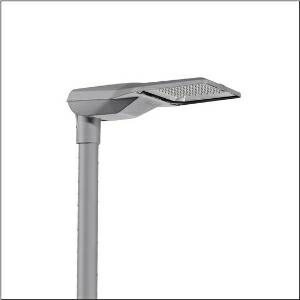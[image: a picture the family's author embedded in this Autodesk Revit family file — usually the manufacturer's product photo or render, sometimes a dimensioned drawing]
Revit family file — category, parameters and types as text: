
# Revit family: streetlight_sl_21_iq_midi___stw1_0a_5xe3e61d08nb_dcea
name_source: partatom
category: Lighting Fixtures
units: mm (PartAtom-declared; Revit-internal decimal feet)

## family parameters
Cut with Voids When Loaded = No
Host = Face
Light Source = No
Part Type = Normal
Room Calculation Point = No
Round Connector Dimension = Use Diameter
Shared = No

## types (1)
- --- (1 x LED, 20820 lm, 155.5 W, 2700K)
    Apparent Load = 155 VA
    CIE Flux Codes = 39 75 98 100 100
    Color Rendering = 70
    Color Temperature = 2700K
    Default Elevation = 1800 mm
    Description = Streetlight SL 21 iQ midi, mast luminaire, primary light control with lens, of PMMA, primary optical cover: cover, of toughened safety glass, transparent, light distribution: STW1.0a, light emission: direct distribution, primary light characteristic: asymmetric, installation type: post-top, side-entry, LED, High Power LED, rated luminous flux: 20.820lm, luminous efficacy: 134lm/W, light colour: 727, colour temperature: 2700K, control gear: iQ-Comfort, control: Auto-Match, Temp-Guard, Lumen-Switch, Night-Set, Smart-Wire, Light-Fading, Desk-Remote (wireless, voltage-free reading and setting of iQ features in the workshop via application-optimized NFC function/RFID function), optimised constant luminous flux control (CLO 2.0), pre-setting: linear dimming characteristic, mains connection: 230..240V, AC, 50/60Hz, start of lifetime: 156W, end of service life: 162W, reduction: 69W, luminaire housing, of diecast aluminium, powder-coated, Siteco® metallic grey (DB 702S), corrosivity category C5 mid according to DIN EN ISO 12944, please order mast flange separately, inclination adjustable: 0°, 5°, 10°, 15°, sealing non-destructively replaceable, multi-level sealing system, length: 644mm, width: 335mm, height: 110mm, mast flange for spigot size: 42mm (side-entry): 5XC10008XM4, 60/48mm (side-entry/post-top): 5XC10108XM2, 76/60mm (side-entry/post-top): 5XC10108XM1, mounting height: 4..8m, protection rating (complete): IP66, insulation class (complete): insulation class II (safety insulation), certification: CE, ENEC, ENEC+, VDE, impact resistance: IK10, permissible operating ambient temperature for outdoor applications: -40..+50°C, standard-compliant lighting for roads and squares, packaging unit: 1 piece

Light Distribution: STW1.0a
    Height = 111 mm
    Lamp = 1 x LED
    Lamp Light Flux = 20820 lm
    Lamp Power = 155.5 W
    Lamp count = 1
    Length = 644 mm
    Luminous efficacy = 134 lm/W
    Manufacturer = Siteco
    ModVariant = No
    Model = 5XE3E61D08NB
    Number of Poles = 1
    OnlyDefault = Yes
    Power Factor = 1
    Product Name = Streetlight SL 21 iQ midi | STW1.0a
    Product group = mast luminaire | pylon top
    ProductGroupID = 6100
    Protection Class = Protection class II
    Protection Degree = IP 66
    RLX_Detail_Level = 1
    RLX_Emergency_Light_Flux = 0 lm
    RLX_Emergency_Type = 0
    RLX_Emergency_Type_DB = No
    RlxData = <blob elided: 27261 chars, md5=28bb8641>
    Socket = socket
    Standby Power = 0 W
    System Light Flux = 20820 lm
    System Power = 155 W
    Type Comments = factory setting: luminous flux: 100 % | dim-lin: 254 | 823 mA
    Type Image = l_1004298.jpg
    URL = http://relux.com
    VarID = @adj_191229
    Voltage = 0 V
    Weight = 0.00 kg
    Width = 336 mm

## geometry (parser evidence)
native form markers: Blend x4, Sweep x10
no freeform markers — native parametric forms only
